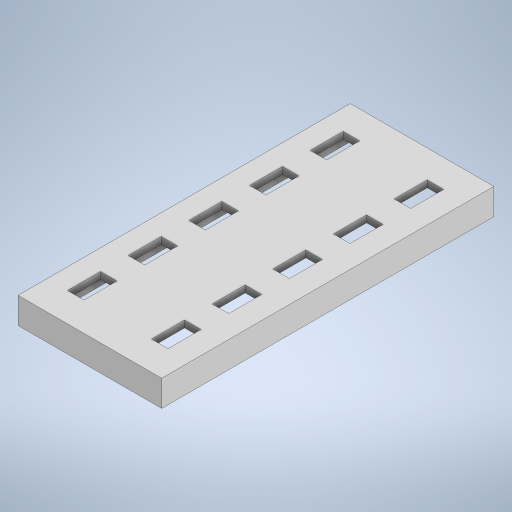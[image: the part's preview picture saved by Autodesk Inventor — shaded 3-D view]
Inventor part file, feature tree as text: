
AUTODESK INVENTOR PART (.ipt)
format: ipt  version: 2024 (Build 280153000, 153)  size: 335,360 bytes
history: native  units: in
note: dims shown in document units (in); Inventor stores cm internally (conversion verified against a paired STEP export)
features: extrude x2, sketch x2, projected_geometry x2
ambient origin geometry x8: Origin, YZ Plane, XZ Plane, XY Plane, X Axis, Y Axis, Z Axis, Center Point
bodies: Body1 (feature_tree)
feature tree (6):
  extrude  "Extrusion4"  Depth=5.753in
  extrude  "Extrusion5"  Depth=0.125in
  sketch  "Sketch4"  dims[d503=2.353in d504=5.753in]
  sketch  "Sketch5"  dims[d505=0.247in d506=0.377in d507=0.3in d508=0.6in d509=0.5in d510=0.3in d511=0.6in d512=0.5in d513=0.3in d514=0.6in d515=0.5in d516=0.3in d517=0.6in d518=0.5in d519=0.3in d520=0.6in d521=0.282in d522=0.377in d523=0.125in d524=0.0in d526=0.35in d527=0.0in d529=0.125in d530=0.02in d531=0.125in d532=0.125in]
  projected_geometry  "Projected Loop2"
  projected_geometry  "Projected Loop3"
